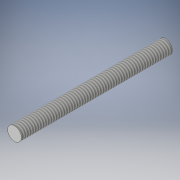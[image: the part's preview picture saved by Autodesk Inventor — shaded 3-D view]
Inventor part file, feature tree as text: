
AUTODESK INVENTOR PART (.ipt)
format: ipt  version: 2017 (Build 210142000, 142)  size: 100,352 bytes
history: native  units: in
note: dims shown in document units (in); Inventor stores cm internally (conversion verified against a paired STEP export)
features: extrude x2, sketch x2, thread x1
ambient origin geometry x8: Origin, YZ Plane, XZ Plane, XY Plane, X Axis, Y Axis, Z Axis, Center Point
bodies: Solid1 (feature_tree)
feature tree (5):
  extrude  "Extrusion1"  Depth=3.0in TaperAngle=0.0deg
  thread  "Thread1"  [1 undecoded]
  extrude  "Extrusion2"  [1 undecoded]
  sketch  "Sketch1"  dims[d0=0.164in d1=3.0in d2=0.0in d3=1.0in d4=0.0in]
  sketch  "Sketch2"  dims[d5=1.811in d6=0.0in]
note: 2 required parameter values undecoded (feature->parameter linkage not recoverable at this tier; creation-order binding heuristic only, values carry confidence <= 0.55)
